# Revit family: BSCH
name_source: partatom
category: Air Terminals
revit_build: Autodesk Revit MEP 2012 (Build: 20110309_2315(x64)
units: mm (PartAtom-declared; Revit-internal decimal feet)

## types (4) — shared parameters
Altura = 1 1/2"
Largo aspas = 18 7/16"
Manufacturer = INNE
Máxima presión estática = 0.00 in-wg
Máxima velocidad de cuello = 0 FPM
Mínima presión estática = 0.00 in-wg
Mínima velocidad de cuello = 0 FPM
Separacion = 1"
URL = http://www.inne.com.mx

## per-type parameters (varying)
| type | A Largo | B Alto | B marco | Height | No. de elementos | Width |
| BSCH-18-16 | 17 7/16" | 15 7/16" | 17 7/16" | 16 15/16" | 15 | 18 15/16" |
| BSCH-20-18 | 19 7/16" | 17 7/16" | 19 7/16" | 18 15/16" | 17 | 20 15/16" |
| BSCH-22-20 | 21 7/16" | 19 7/16" | 21 7/16" | 20 15/16" | 19 | 22 15/16" |
| BSCH-24-22 | 23 7/16" | 21 7/16" | 23 7/16" | 22 15/16" | 21 | 24 15/16" |

## geometry (parser evidence)
native form markers: Sweep x2
no freeform markers — native parametric forms only
